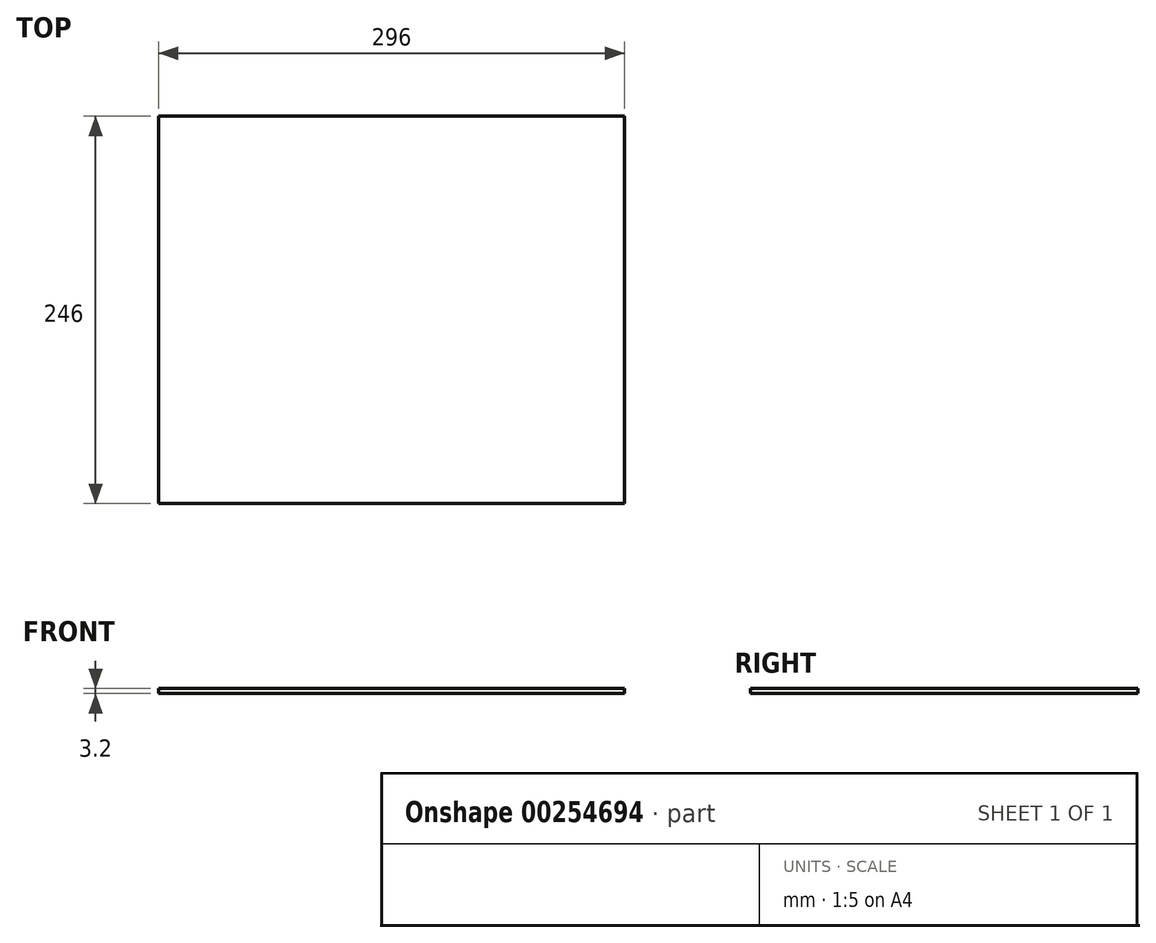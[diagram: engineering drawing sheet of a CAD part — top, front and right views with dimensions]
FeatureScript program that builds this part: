
annotation { "Feature Type Name" : "Feature", "Feature Type Description" : "" }
export const myFeature = defineFeature(function(context is Context, id is Id, definition is map)
    precondition{}
    {
        {
            var Q0;
            Q0=qCreatedBy(makeId("Top.planeOp"),FACE);
            var sketch = newSketch(context, id + "F0", { "sketchPlane" : qUnion([Q0])});
            skLineSegment(sketch, "E0.bottom", {"start": v(0, 0) * mm, "end": v(296, 0) * mm});
            skLineSegment(sketch, "E0.top", {"start": v(0, 246) * mm, "end": v(296, 246) * mm});
            skLineSegment(sketch, "E0.left", {"start": v(0, 0) * mm, "end": v(0, 246) * mm});
            skLineSegment(sketch, "E0.right", {"start": v(296, 0) * mm, "end": v(296, 246) * mm});
            skSolve(sketch);
        }
        {
            var Q0;
            Q0=qSketchRegion(id+"F0",true);
            extrude(context, id + "F1", {"entities" : qUnion([Q0]), "depth" : 3.2 * mm});
        }
    });
